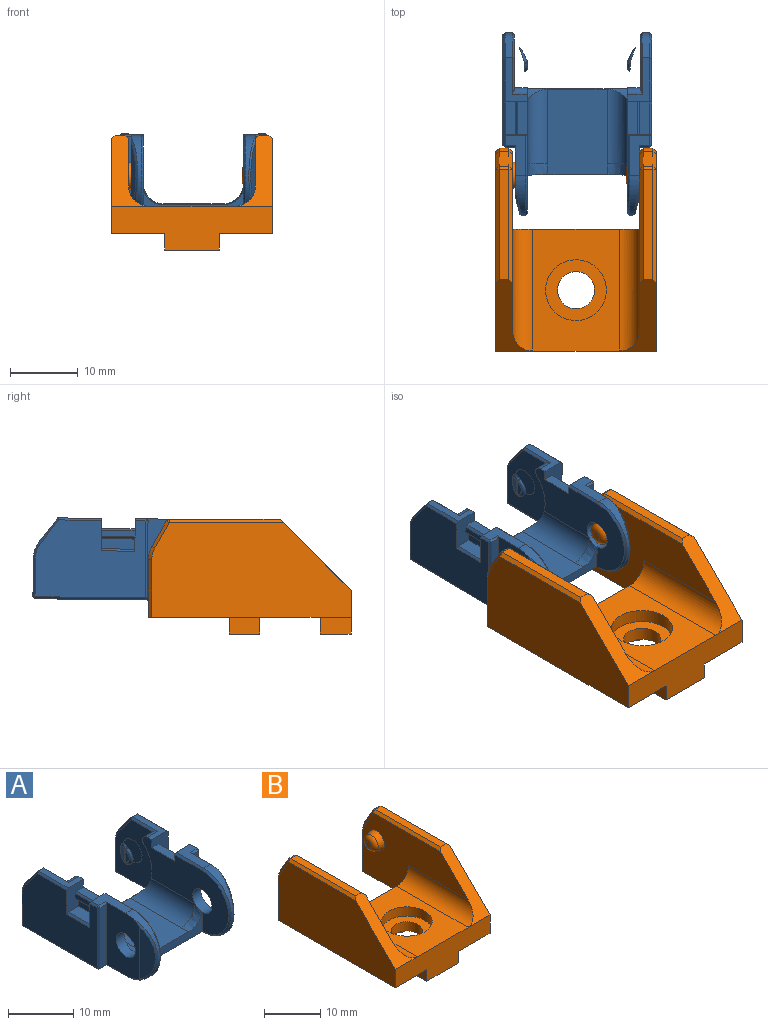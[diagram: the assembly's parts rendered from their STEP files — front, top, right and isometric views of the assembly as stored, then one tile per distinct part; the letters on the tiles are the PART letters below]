
ASSEMBLY  parts=2 mates=1
PART A: 125 faces, bbox 22.1x27.1x12.1 mm
  f0: plane 11.72x7.47mm, normal (1,0,0), area 67.9mm2, adj f1,f4,f12,f14,f28,f31,f32,f33
  f1: cylinder r=6mm len=12mm, axis (-1,0,0), area 18mm2, adj f0,f4,f6,f31,f32,f56
  f2: plane 2.18x0.83mm, normal (-1,0,0), area 1.3mm2, adj f62,f65
  f3: cone r=2mm half-angle=15deg, axis (1,0,0), area 15mm2, adj f18,f61,f62
  f4: plane 6x3mm, normal (0,0,1), area 11.4mm2, adj f0,f1,f25,f33,f34,f57
  f5: plane 16.3x11.4mm, normal (1,0,0), area 155.6mm2, adj f24,f25,f34,f37,f39,f40,f42,f43
  f6: plane 21.4x20.7mm, normal (0,0,-1), area 263.5mm2, adj f1,f35,f38,f43,f45,f47,f48,f54
  f7: plane 18.6x1.36mm, normal (0,1,0), area 25.3mm2, adj f10,f18,f45,f79
  f8: plane 12.67x9.02mm, normal (0,0,1), area 111.7mm2, adj f9,f10,f29,f30,f90,f91
  f9: plane 14.85x3.65mm, normal (0,-1,0), area 24mm2, adj f8,f13,f29,f54,f74,f90
  f10: cylinder r=6.1mm len=18.6mm, axis (-1,0,0), area 47.7mm2, adj f7,f8,f13,f18,f26,f30,f74,f79
  f11: plane 6.44x3.3mm, normal (0,0,1), area 9.2mm2, adj f13,f17,f24,f26,f37,f52
  f12: cylinder r=2.1mm len=4.2mm, axis (-1,0,0), area 23.8mm2, adj f0,f13,f29
  f13: plane 18.66x11.7mm, normal (-1,0,0), area 114mm2, adj f9,f10,f11,f12,f19,f24,f25,f26
  f14: plane 11.4x1.5mm, normal (0,-1,0), area 17.1mm2, adj f0,f33,f38,f39
  f15: plane 5.7x1.1mm, normal (0,1,0), area 6.3mm2, adj f16,f44,f48,f50
  f16: cylinder r=4mm len=2.44mm, axis (-1,0,0), area 2.9mm2, adj f15,f17,f42,f51
  f17: plane 3.57x2.74mm, normal (0,0.79,0.61), area 4.9mm2, adj f11,f16,f40,f53
  f18: plane 11.4x9.8mm, normal (-1,0,0), area 81mm2, adj f3,f7,f10,f26,f47,f50,f51,f52
  f19: plane 5x1.5mm, normal (0,0,1), area 7.5mm2, adj f13,f24,f25,f58
  f20: plane 5x0.9mm, normal (1,0,0), area 4.5mm2, adj f24,f25,f58,f59
  f21: plane 5x0.4mm, normal (0,0,-1), area 2mm2, adj f22,f24,f25,f59
  f22: plane 5x1.5mm, normal (1,0,0), area 7.5mm2, adj f21,f23,f24,f25
  f23: plane 5x2.2mm, normal (0,0,1), area 11mm2, adj f22,f24,f25,f60
  f24: plane 4.8x3.6mm, normal (0,-1,0), area 11.9mm2, adj f5,f11,f13,f19,f20,f21,f22,f23
  f25: plane 4.8x3.6mm, normal (0,1,0), area 11.9mm2, adj f4,f5,f13,f19,f20,f21,f22,f23
  f26: cylinder r=1mm len=2.2mm, axis (-1,0,0), area 4.6mm2, adj f10,f11,f13,f18,f52
  f27: plane 2.37x1.66mm, normal (-0.9,0.43,0), area 3.7mm2, adj f61,f65
  f28: plane 9.7x2.77mm, normal (0.97,-0.25,0), area 19.4mm2, adj f0,f31,f32
  f29: bspline ~3.18x3.17mm, area 6.9mm2, adj f8,f9,f12,f30
  f30: cylinder r=3mm len=11.02mm, axis (0,1,0), area 48.1mm2, adj f8,f10,f13,f29
  f31: bspline ~10.78x4.1mm, area 4.8mm2, adj f0,f1,f28,f32
  f32: cone r=5.7mm half-angle=45deg, axis (-1,0,0), area 1.4mm2, adj f0,f1,f28,f31,f35
  f33: plane 1.5x0.3mm, normal (0,-0.71,0.71), area 0.6mm2, adj f0,f4,f14,f36
  f34: plane 1.6x0.3mm, normal (0.71,0,0.71), area 0.7mm2, adj f4,f5,f25,f36
  f35: plane 4.4x0.3mm, normal (0.71,0,-0.71), area 1.8mm2, adj f0,f6,f32,f38
  f36: plane 0.3x0.3mm, normal (0.58,-0.58,0.58), area 0.1mm2, adj f33,f34,f39
  f37: plane 6.44x0.3mm, normal (0.71,0,0.71), area 2.7mm2, adj f5,f11,f24,f40
  f38: plane 1.8x0.3mm, normal (0,-0.71,-0.71), area 0.7mm2, adj f6,f14,f35,f41
  f39: plane 11.4x0.3mm, normal (0.71,-0.71,0), area 4.8mm2, adj f5,f14,f36,f41
  f40: plane 3.75x2.88mm, normal (0.71,0.56,0.43), area 1.9mm2, adj f5,f17,f37,f42
  f41: plane 0.3x0.3mm, normal (0.58,-0.58,-0.58), area 0.1mm2, adj f38,f39,f43
  f42: cone r=3.7mm half-angle=45deg, axis (-1,0,0), area 1.1mm2, adj f5,f16,f40,f44
  f43: plane 16.3x0.3mm, normal (0.71,0,-0.71), area 6.9mm2, adj f5,f6,f41,f46
  f44: plane 5.7x0.3mm, normal (0.71,0.71,0), area 2.4mm2, adj f5,f15,f42,f46
  f45: plane 19.2x0.3mm, normal (0,0.71,-0.71), area 8mm2, adj f6,f7,f47,f107
  f46: plane 0.3x0.3mm, normal (0.58,0.58,-0.58), area 0.1mm2, adj f43,f44,f48
  f47: plane 8.28x0.3mm, normal (-0.71,0,-0.71), area 3.5mm2, adj f6,f18,f45,f49
  f48: plane 1.1x0.3mm, normal (0,0.71,-0.71), area 0.5mm2, adj f6,f15,f46,f49
  f49: plane 0.3x0.3mm, normal (-0.58,0.58,-0.58), area 0.1mm2, adj f47,f48,f50
  f50: plane 5.7x0.3mm, normal (-0.71,0.71,0), area 2.4mm2, adj f15,f18,f49,f51
  f51: cone r=4mm half-angle=45deg, axis (1,0,0), area 1.1mm2, adj f16,f18,f50,f53
  f52: plane 5.62x0.44mm, normal (-0.71,0,0.71), area 2.1mm2, adj f11,f18,f26,f53
  f53: plane 3.75x2.88mm, normal (-0.71,0.56,0.43), area 1.9mm2, adj f17,f18,f51,f52
  f54: plane 15.4x0.3mm, normal (0,-0.71,-0.71), area 6.4mm2, adj f6,f9,f55,f114
  f55: plane 0.3x0.3mm, normal (-0.71,0,-0.71), area 0.1mm2, adj f6,f54,f56
  f56: cone r=6mm half-angle=45deg, axis (1,0,0), area 7.8mm2, adj f1,f13,f55,f57
  f57: plane 6x0.3mm, normal (-0.71,0,0.71), area 2.5mm2, adj f4,f13,f25,f56
  f58: plane 5x0.3mm, normal (0.71,0,0.71), area 2.1mm2, adj f19,f20,f24,f25
  f59: plane 5x0.3mm, normal (0.71,0,-0.71), area 2.1mm2, adj f20,f21,f24,f25
  f60: plane 5x0.3mm, normal (0.71,0,0.71), area 2.1mm2, adj f5,f23,f24,f25
  f61: bspline ~3.33x2.27mm, area 3.2mm2, adj f3,f27,f63,f64
  f62: torus R=1.13mm, axis (1,0,0), area 2.4mm2, adj f2,f3,f63,f64
  f63: sphere r=0.5mm, area 0.1mm2, adj f61,f62,f65
  f64: sphere r=0.5mm, area 0.1mm2, adj f61,f62,f65
  f65: cylinder r=0.5mm len=2.18mm, axis (0,0,-1), area 0.5mm2, adj f2,f27,f63,f64
  f66: plane 11.72x7.47mm, normal (-1,0,0), area 67.9mm2, adj f67,f70,f73,f75,f89,f92,f93,f94
  f67: cylinder r=6mm len=12mm, axis (1,0,0), area 18mm2, adj f6,f66,f70,f92,f93,f115
  f68: plane 2.18x0.83mm, normal (1,0,0), area 1.3mm2, adj f121,f124
  f69: cone r=2mm half-angle=15deg, axis (-1,0,0), area 15mm2, adj f79,f120,f121
  f70: plane 6x3mm, normal (0,0,1), area 11.4mm2, adj f66,f67,f86,f94,f95,f116
  f71: plane 16.3x11.4mm, normal (-1,0,0), area 155.6mm2, adj f85,f86,f95,f98,f100,f101,f103,f104
  f72: plane 6.44x3.3mm, normal (0,0,1), area 9.2mm2, adj f74,f78,f85,f87,f98,f112
  f73: cylinder r=2.1mm len=4.2mm, axis (1,0,0), area 23.8mm2, adj f66,f74,f90
  f74: plane 18.66x11.7mm, normal (1,0,0), area 114mm2, adj f9,f10,f72,f73,f80,f85,f86,f87
  f75: plane 11.4x1.5mm, normal (0,-1,0), area 17.1mm2, adj f66,f94,f99,f100
  f76: plane 5.7x1.1mm, normal (0,1,0), area 6.3mm2, adj f77,f105,f108,f110
  f77: cylinder r=4mm len=2.44mm, axis (1,0,0), area 2.9mm2, adj f76,f78,f103,f111
  f78: plane 3.57x2.74mm, normal (0,0.79,0.61), area 4.9mm2, adj f72,f77,f101,f113
  f79: plane 11.4x9.8mm, normal (1,0,0), area 81mm2, adj f7,f10,f69,f87,f107,f110,f111,f112
  f80: plane 5x1.5mm, normal (0,0,1), area 7.5mm2, adj f74,f85,f86,f117
  f81: plane 5x0.9mm, normal (-1,0,0), area 4.5mm2, adj f85,f86,f117,f118
  f82: plane 5x0.4mm, normal (0,0,-1), area 2mm2, adj f83,f85,f86,f118
  f83: plane 5x1.5mm, normal (-1,0,0), area 7.5mm2, adj f82,f84,f85,f86
  f84: plane 5x2.2mm, normal (0,0,1), area 11mm2, adj f83,f85,f86,f119
  f85: plane 4.8x3.6mm, normal (0,-1,0), area 11.9mm2, adj f71,f72,f74,f80,f81,f82,f83,f84
  f86: plane 4.8x3.6mm, normal (0,1,0), area 11.9mm2, adj f70,f71,f74,f80,f81,f82,f83,f84
  f87: cylinder r=1mm len=2.2mm, axis (1,0,0), area 4.6mm2, adj f10,f72,f74,f79,f112
  f88: plane 2.37x1.66mm, normal (0.9,0.43,0), area 3.7mm2, adj f120,f124
  f89: plane 9.7x2.77mm, normal (-0.97,-0.25,0), area 19.4mm2, adj f66,f92,f93
  f90: bspline ~3.18x3.17mm, area 6.9mm2, adj f8,f9,f73,f91
  f91: cylinder r=3mm len=11.02mm, axis (0,1,0), area 48.1mm2, adj f8,f10,f74,f90
  f92: bspline ~10.78x4.1mm, area 4.8mm2, adj f66,f67,f89,f93
  f93: cone r=5.7mm half-angle=45deg, axis (1,0,0), area 1.4mm2, adj f66,f67,f89,f92,f96
  f94: plane 1.5x0.3mm, normal (0,-0.71,0.71), area 0.6mm2, adj f66,f70,f75,f97
  f95: plane 1.6x0.3mm, normal (-0.71,0,0.71), area 0.7mm2, adj f70,f71,f86,f97
  f96: plane 4.4x0.3mm, normal (-0.71,0,-0.71), area 1.8mm2, adj f6,f66,f93,f99
  f97: plane 0.3x0.3mm, normal (-0.58,-0.58,0.58), area 0.1mm2, adj f94,f95,f100
  f98: plane 6.44x0.3mm, normal (-0.71,0,0.71), area 2.7mm2, adj f71,f72,f85,f101
  f99: plane 1.8x0.3mm, normal (0,-0.71,-0.71), area 0.7mm2, adj f6,f75,f96,f102
  f100: plane 11.4x0.3mm, normal (-0.71,-0.71,0), area 4.8mm2, adj f71,f75,f97,f102
  f101: plane 3.75x2.88mm, normal (-0.71,0.56,0.43), area 1.9mm2, adj f71,f78,f98,f103
  f102: plane 0.3x0.3mm, normal (-0.58,-0.58,-0.58), area 0.1mm2, adj f99,f100,f104
  f103: cone r=3.7mm half-angle=45deg, axis (1,0,0), area 1.1mm2, adj f71,f77,f101,f105
  f104: plane 16.3x0.3mm, normal (-0.71,0,-0.71), area 6.9mm2, adj f6,f71,f102,f106
  f105: plane 5.7x0.3mm, normal (-0.71,0.71,0), area 2.4mm2, adj f71,f76,f103,f106
  f106: plane 0.3x0.3mm, normal (-0.58,0.58,-0.58), area 0.1mm2, adj f104,f105,f108
  f107: plane 8.28x0.3mm, normal (0.71,0,-0.71), area 3.5mm2, adj f6,f45,f79,f109
  f108: plane 1.1x0.3mm, normal (0,0.71,-0.71), area 0.5mm2, adj f6,f76,f106,f109
  f109: plane 0.3x0.3mm, normal (0.58,0.58,-0.58), area 0.1mm2, adj f107,f108,f110
  f110: plane 5.7x0.3mm, normal (0.71,0.71,0), area 2.4mm2, adj f76,f79,f109,f111
  f111: cone r=4mm half-angle=45deg, axis (-1,0,0), area 1.1mm2, adj f77,f79,f110,f113
  f112: plane 5.62x0.44mm, normal (0.71,0,0.71), area 2.1mm2, adj f72,f79,f87,f113
  f113: plane 3.75x2.88mm, normal (0.71,0.56,0.43), area 1.9mm2, adj f78,f79,f111,f112
  f114: plane 0.3x0.3mm, normal (0.71,0,-0.71), area 0.1mm2, adj f6,f54,f115
  f115: cone r=6mm half-angle=45deg, axis (-1,0,0), area 7.8mm2, adj f67,f74,f114,f116
  f116: plane 6x0.3mm, normal (0.71,0,0.71), area 2.5mm2, adj f70,f74,f86,f115
  f117: plane 5x0.3mm, normal (-0.71,0,0.71), area 2.1mm2, adj f80,f81,f85,f86
  f118: plane 5x0.3mm, normal (-0.71,0,-0.71), area 2.1mm2, adj f81,f82,f85,f86
  f119: plane 5x0.3mm, normal (-0.71,0,0.71), area 2.1mm2, adj f71,f84,f85,f86
  f120: bspline ~3.33x2.27mm, area 3.2mm2, adj f69,f88,f122,f123
  f121: torus R=1.13mm, axis (-1,0,0), area 2.4mm2, adj f68,f69,f122,f123
  f122: sphere r=0.5mm, area 0.1mm2, adj f120,f121,f124
  f123: sphere r=0.5mm, area 0.1mm2, adj f120,f121,f124
  f124: cylinder r=0.5mm len=2.18mm, axis (0,0,-1), area 0.5mm2, adj f68,f88,f122,f123
PART B: 59 faces, bbox 23.8x30x17 mm
  f0: plane 30x23.8mm, normal (0,0,-1), area 408.4mm2, adj f1,f2,f3,f5,f10,f13,f15,f25
  f1: cylinder r=2.75mm len=5.5mm, axis (0,0,1), area 34.6mm2, adj f0,f48
  f2: plane 8.5x1.46mm, normal (0,1,0), area 12.4mm2, adj f0,f7,f15,f25
  f3: plane 23.8x6.5mm, normal (0,-1,0), area 115.2mm2, adj f0,f4,f6,f10,f28,f32,f49,f51
  f4: plane 18x12.8mm, normal (0,0,1), area 166.8mm2, adj f3,f13,f14,f35,f47
  f5: plane 26.48x13.98mm, normal (-1,0,0), area 222.2mm2, adj f0,f6,f11,f13,f14,f15,f16,f17
  f6: plane 10.5x10.5mm, normal (0,-0.71,0.71), area 39.5mm2, adj f3,f5,f9,f10,f14,f17,f20
  f7: cylinder r=4mm len=2mm, axis (-1,0,0), area 3.1mm2, adj f2,f8,f16,f24
  f8: plane 3.74x2.16mm, normal (0,0.87,0.5), area 6.3mm2, adj f7,f18,f21,f23
  f9: plane 16.35x1.46mm, normal (0,0,1), area 23.9mm2, adj f6,f17,f20,f21
  f10: plane 29.48x13.98mm, normal (1,0,0), area 356.3mm2, adj f0,f3,f6,f20,f23,f24,f25
  f11: cone r=2mm half-angle=15deg, axis (1,0,0), area 15mm2, adj f5,f58
  f12: plane 1.39x1.39mm, normal (-1,0,0), area 1.5mm2, adj f58
  f13: plane 18.8x9.5mm, normal (0,1,0), area 99.1mm2, adj f0,f4,f5,f14,f27,f35,f53,f55
  f14: cylinder r=3mm len=18mm, axis (0,-1,0), area 79.7mm2, adj f4,f5,f6,f13
  f15: plane 8.5x0.52mm, normal (-0.71,0.71,0), area 6.2mm2, adj f0,f2,f5,f16
  f16: cone r=4mm half-angle=45deg, axis (1,0,0), area 1.4mm2, adj f5,f7,f15,f18
  f17: plane 16.87x0.52mm, normal (-0.71,0,0.71), area 12.2mm2, adj f5,f6,f9,f19
  f18: plane 4x2.61mm, normal (-0.71,0.61,0.35), area 3.2mm2, adj f5,f8,f16,f19
  f19: plane 0.52x0.52mm, normal (-0.65,0.38,0.65), area 0.2mm2, adj f17,f18,f21
  f20: plane 16.87x0.52mm, normal (0.71,0,0.71), area 12.2mm2, adj f6,f9,f10,f22
  f21: plane 1.46x0.45mm, normal (0,0.5,0.87), area 0.8mm2, adj f8,f9,f19,f22
  f22: plane 0.52x0.52mm, normal (0.65,0.38,0.65), area 0.2mm2, adj f20,f21,f23
  f23: plane 4x2.61mm, normal (0.71,0.61,0.35), area 3.2mm2, adj f8,f10,f22,f24
  f24: cone r=3.48mm half-angle=45deg, axis (-1,0,0), area 1.4mm2, adj f7,f10,f23,f25
  f25: plane 8.5x0.52mm, normal (0.71,0.71,0), area 6.2mm2, adj f0,f2,f10,f24
  f26: plane 8.5x1.46mm, normal (0,1,0), area 12.4mm2, adj f0,f29,f36,f46
  f27: plane 26.48x13.98mm, normal (1,0,0), area 222.2mm2, adj f0,f13,f28,f33,f35,f36,f37,f38
  f28: plane 10.5x10.5mm, normal (0,-0.71,0.71), area 39.5mm2, adj f3,f27,f31,f32,f35,f38,f41
  f29: cylinder r=4mm len=2mm, axis (1,0,0), area 3.1mm2, adj f26,f30,f37,f45
  f30: plane 3.74x2.16mm, normal (0,0.87,0.5), area 6.3mm2, adj f29,f39,f42,f44
  f31: plane 16.35x1.46mm, normal (0,0,1), area 23.9mm2, adj f28,f38,f41,f42
  f32: plane 29.48x13.98mm, normal (-1,0,0), area 356.3mm2, adj f0,f3,f28,f41,f44,f45,f46
  f33: cone r=2mm half-angle=15deg, axis (-1,0,0), area 15mm2, adj f27,f57
  f34: plane 1.39x1.39mm, normal (1,0,0), area 1.5mm2, adj f57
  f35: cylinder r=3mm len=18mm, axis (0,-1,0), area 79.7mm2, adj f4,f13,f27,f28
  f36: plane 8.5x0.52mm, normal (0.71,0.71,0), area 6.2mm2, adj f0,f26,f27,f37
  f37: cone r=4mm half-angle=45deg, axis (-1,0,0), area 1.4mm2, adj f27,f29,f36,f39
  f38: plane 16.87x0.52mm, normal (0.71,0,0.71), area 12.2mm2, adj f27,f28,f31,f40
  f39: plane 4x2.61mm, normal (0.71,0.61,0.35), area 3.2mm2, adj f27,f30,f37,f40
  f40: plane 0.52x0.52mm, normal (0.65,0.38,0.65), area 0.2mm2, adj f38,f39,f42
  f41: plane 16.87x0.52mm, normal (-0.71,0,0.71), area 12.2mm2, adj f28,f31,f32,f43
  f42: plane 1.46x0.45mm, normal (0,0.5,0.87), area 0.8mm2, adj f30,f31,f40,f43
  f43: plane 0.52x0.52mm, normal (-0.65,0.38,0.65), area 0.2mm2, adj f41,f42,f44
  f44: plane 4x2.61mm, normal (-0.71,0.61,0.35), area 3.2mm2, adj f30,f32,f43,f45
  f45: cone r=3.48mm half-angle=45deg, axis (1,0,0), area 1.4mm2, adj f29,f32,f44,f46
  f46: plane 8.5x0.52mm, normal (-0.71,0.71,0), area 6.2mm2, adj f0,f26,f32,f45
  f47: cylinder r=4.5mm len=9mm, axis (0,0,1), area 56.5mm2, adj f4,f48
  f48: plane 9x9mm, normal (0,0,1), area 39.9mm2, adj f1,f47
  f49: plane 4.53x2.5mm, normal (-1,0,0), area 11.3mm2, adj f0,f3,f50,f52
  f50: cylinder r=6mm len=8mm, axis (0,0,1), area 21.9mm2, adj f0,f49,f51,f52
  f51: plane 4.53x2.5mm, normal (1,0,0), area 11.3mm2, adj f0,f3,f50,f52
  f52: plane 8x4.53mm, normal (0,0,-1), area 27.8mm2, adj f3,f49,f50,f51
  f53: plane 4.53x2.5mm, normal (1,0,0), area 11.3mm2, adj f0,f13,f54,f56
  f54: cylinder r=6mm len=8mm, axis (0,0,1), area 21.9mm2, adj f0,f53,f55,f56
  f55: plane 4.53x2.5mm, normal (-1,0,0), area 11.3mm2, adj f0,f13,f54,f56
  f56: plane 8x4.53mm, normal (0,0,-1), area 27.8mm2, adj f13,f53,f54,f55
  f57: torus R=0.7mm, axis (-1,0,0), area 10.4mm2, adj f33,f34
  f58: torus R=0.7mm, axis (1,0,0), area 10.4mm2, adj f11,f12
PLACE A rot(axis=(1,0,0),0.6deg) t=(78.87,148.45,30.86)mm
PLACE B t=(78.67,139.38,30.72)mm fixed
MATE revolute A.f1 <-> B.f7  axis (1,0,0) through (88.07,135.38,36.72)mm
